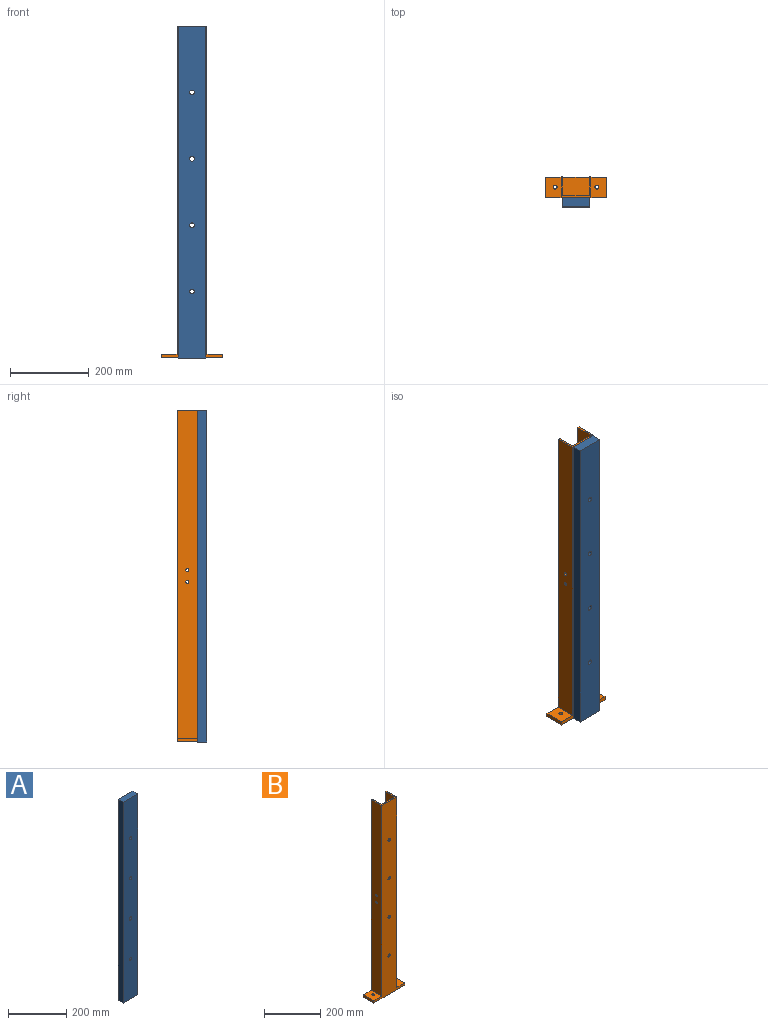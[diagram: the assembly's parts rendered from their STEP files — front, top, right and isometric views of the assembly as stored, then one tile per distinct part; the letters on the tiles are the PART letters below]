
ASSEMBLY  parts=2 mates=1
PART A: 10 faces, bbox 70x24x841.5 mm
  f0: plane 70x24mm, normal (0,0,1), area 1680mm2, adj f1,f3,f4,f5
  f1: plane 841.5x24mm, normal (-1,0,0), area 20196mm2, adj f0,f2,f4,f5
  f2: plane 70x24mm, normal (0,0,-1), area 1680mm2, adj f1,f3,f4,f5
  f3: plane 841.5x24mm, normal (1,0,0), area 20196mm2, adj f0,f2,f4,f5
  f4: plane 841.5x70mm, normal (0,-1,0), area 58452.6mm2, adj f0,f1,f2,f3,f6,f7,f8,f9
  f5: plane 841.5x70mm, normal (0,1,0), area 58452.6mm2, adj f0,f1,f2,f3,f6,f7,f8,f9
  f6: cylinder r=6mm len=24mm, axis (0,-1,0), area 904.8mm2, adj f4,f5
  f7: cylinder r=6mm len=24mm, axis (0,-1,0), area 904.8mm2, adj f4,f5
  f8: cylinder r=6mm len=24mm, axis (0,-1,0), area 904.8mm2, adj f4,f5
  f9: cylinder r=6mm len=24mm, axis (0,-1,0), area 904.8mm2, adj f4,f5
PART B: 24 faces, bbox 156x52x841.5 mm
  f0: plane 831.5x52mm, normal (-1,0,0), area 43137.5mm2, adj f1,f3,f7,f9,f10,f20
  f1: plane 841.5x156mm, normal (0,-1,0), area 64301.6mm2, adj f0,f2,f7,f8,f13,f14,f15,f16
  f2: plane 831.5x52mm, normal (1,0,0), area 43137.5mm2, adj f1,f3,f7,f11,f12,f19
  f3: plane 841.5x156mm, normal (0,1,0), area 9875mm2, adj f0,f2,f4,f6,f7,f8,f17,f18
  f4: plane 831.5x47mm, normal (-1,0,0), area 38980mm2, adj f3,f5,f7,f11,f12,f17
  f5: plane 831.5x66mm, normal (0,1,0), area 54426.6mm2, adj f4,f6,f7,f13,f14,f15,f16,f17
  f6: plane 831.5x47mm, normal (1,0,0), area 38980mm2, adj f3,f5,f7,f9,f10,f17
  f7: plane 76x52mm, normal (0,0,1), area 850mm2, adj f0,f1,f2,f3,f4,f5,f6
  f8: plane 156x52mm, normal (0,0,-1), area 7954.9mm2, adj f1,f3,f18,f21,f22,f23
  f9: cylinder r=4mm len=8mm, axis (1,0,0), area 125.7mm2, adj f0,f6
  f10: cylinder r=4mm len=8mm, axis (1,0,0), area 125.7mm2, adj f0,f6
  f11: cylinder r=4mm len=8mm, axis (1,0,0), area 125.7mm2, adj f2,f4
  f12: cylinder r=4mm len=8mm, axis (1,0,0), area 125.7mm2, adj f2,f4
  f13: cylinder r=6mm len=12mm, axis (0,-1,0), area 188.5mm2, adj f1,f5
  f14: cylinder r=6mm len=12mm, axis (0,-1,0), area 188.5mm2, adj f1,f5
  f15: cylinder r=6mm len=12mm, axis (0,-1,0), area 188.5mm2, adj f1,f5
  f16: cylinder r=6mm len=12mm, axis (0,-1,0), area 188.5mm2, adj f1,f5
  f17: plane 66x47mm, normal (0,0,1), area 3102mm2, adj f3,f4,f5,f6
  f18: plane 52x10mm, normal (1,0,0), area 520mm2, adj f1,f3,f8,f19
  f19: plane 52x40mm, normal (0,0,1), area 2001.5mm2, adj f1,f2,f3,f18,f23
  f20: plane 52x40mm, normal (0,0,1), area 2001.5mm2, adj f0,f1,f3,f21,f22
  f21: plane 52x10mm, normal (-1,0,0), area 520mm2, adj f1,f3,f8,f20
  f22: cylinder r=5mm len=10mm, axis (0,0,1), area 314.2mm2, adj f8,f20
  f23: cylinder r=5mm len=10mm, axis (0,0,1), area 314.2mm2, adj f8,f19
PLACE A t=(-57.13,70.02,154.48)mm
PLACE B t=(93.51,70.02,178.76)mm
MATE fastened B.f16 <-> A.f9  axis (0,-1,0) through (517.41,-64.43,466.96)mm
